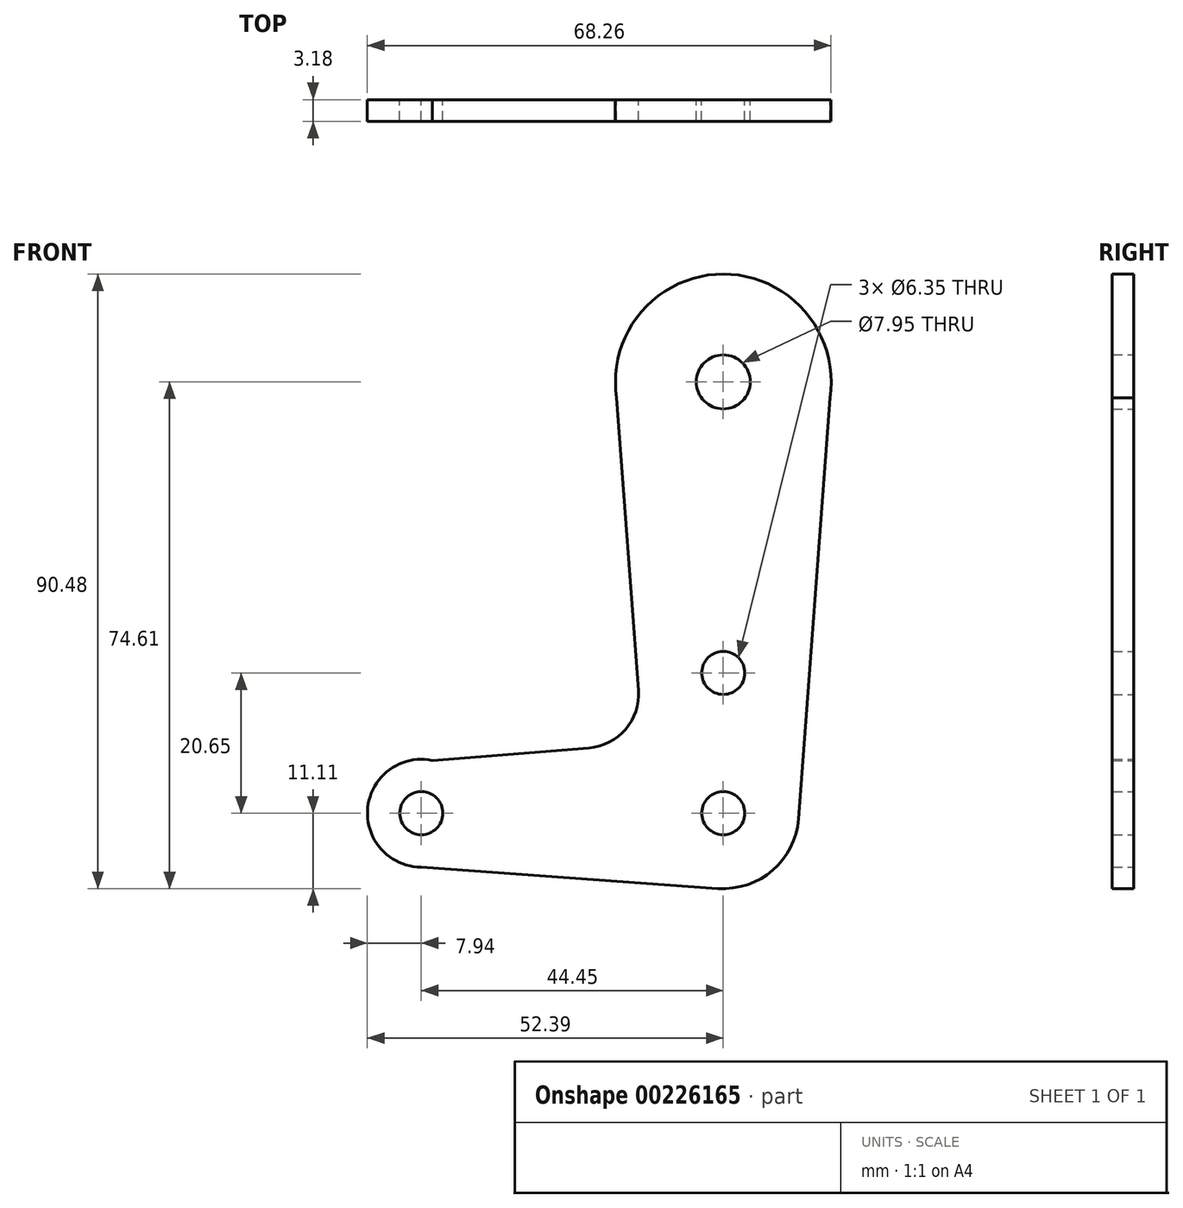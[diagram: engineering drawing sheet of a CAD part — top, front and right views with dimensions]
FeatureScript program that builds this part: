
annotation { "Feature Type Name" : "Feature", "Feature Type Description" : "" }
export const myFeature = defineFeature(function(context is Context, id is Id, definition is map)
    precondition{}
    {
        {
            var Q0;
            Q0=qCreatedBy(makeId("Front.planeOp"),FACE);
            var sketch = newSketch(context, id + "F0", { "sketchPlane" : qUnion([Q0])});
            skArc(sketch, "E0", {"start": v(15.7, -2.35) * mm, "mid": v(0, 15.88) * mm, "end": v(-15.7, -2.35) * mm});
            skLineSegment(sketch, "E1", {"start": v(0, 0) * mm, "end": v(0, -63.5) * mm});
            skArc(sketch, "E2", {"start": v(-0.8, -74.58) * mm, "mid": v(7.26, -71.91) * mm, "end": v(11.08, -64.33) * mm});
            skLineSegment(sketch, "E3", {"start": v(0, -63.5) * mm, "end": v(-44.45, -63.5) * mm});
            skLineSegment(sketch, "E4", {"start": v(0, -63.5) * mm, "end": v(0, -42.85) * mm});
            skCircle(sketch, "E5", {"center": v(0, -42.85) * mm, "radius": 3.18 * mm});
            skArc(sketch, "E6", {"start": v(-42.83, -55.73) * mm, "mid": v(-52.34, -62.67) * mm, "end": v(-44.47, -71.44) * mm});
            skLineSegment(sketch, "E7", {"start": v(-15.87, 0) * mm, "end": v(-12.5, -45.4) * mm});
            skLineSegment(sketch, "E8", {"start": v(-42.83, -55.73) * mm, "end": v(-19.8, -53.91) * mm});
            skLineSegment(sketch, "E9", {"start": v(-44.47, -71.44) * mm, "end": v(0, -74.64) * mm});
            skLineSegment(sketch, "E10", {"start": v(15.88, 0) * mm, "end": v(11.08, -64.33) * mm});
            skCircle(sketch, "E11", {"center": v(0, 0) * mm, "radius": 3.98 * mm});
            skCircle(sketch, "E12", {"center": v(-44.45, -63.5) * mm, "radius": 3.18 * mm});
            skCircle(sketch, "E13", {"center": v(0, -63.5) * mm, "radius": 3.18 * mm});
            skCircle(sketch, "E14", {"center": v(0, 0) * mm, "radius": 3.18 * mm});
            skArc(sketch, "E15.filletArc", {"start": v(-19.8, -53.91) * mm, "mid": v(-14.39, -51.16) * mm, "end": v(-12.5, -45.4) * mm});
            skSolve(sketch);
        }
        {
            var Q0;
            Q0 = qSketchRegion(id + "F0", true);
            extrude(context, id + "F1", {"entities" : qUnion([Q0]), "depth" : 3.17 * mm});
        }
    });
